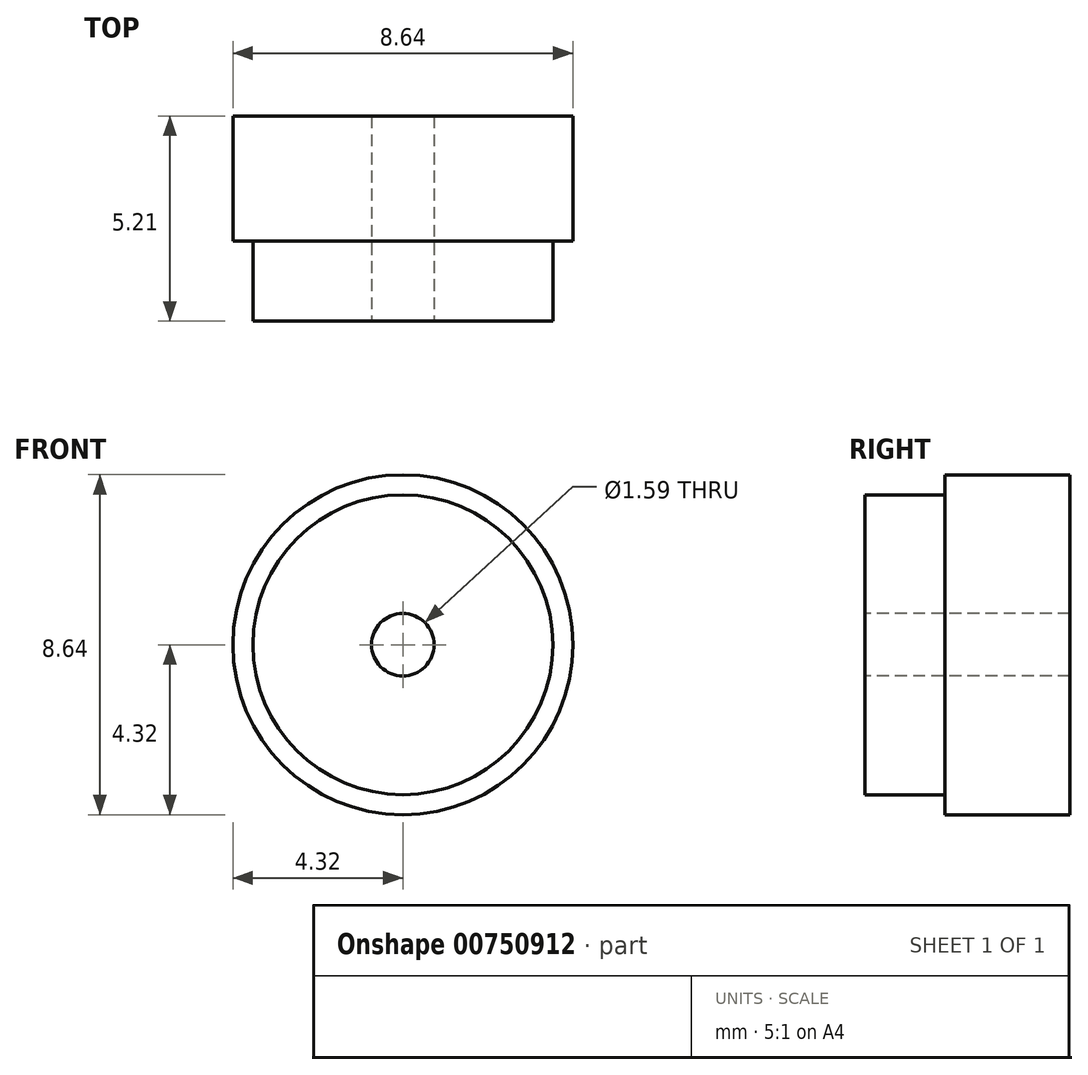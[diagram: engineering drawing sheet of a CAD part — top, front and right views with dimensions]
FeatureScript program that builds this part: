
annotation { "Feature Type Name" : "Feature", "Feature Type Description" : "" }
export const myFeature = defineFeature(function(context is Context, id is Id, definition is map)
    precondition{}
    {
        {
            var Q0;
            Q0=qCreatedBy(makeId("Front.planeOp"),FACE);
            var sketch = newSketch(context, id + "F0", { "sketchPlane" : qUnion([Q0])});
            skCircle(sketch, "E0", {"center": v(0, 0) * mm, "radius": 4.32 * mm});
            skSolve(sketch);
        }
        {
            var Q0;
            Q0 = qSketchRegion(id + "F0", true);
            extrude(context, id + "F1", {"entities" : qUnion([Q0]), "oppositeDirection" : true, "depth" : 3.17 * mm, "offsetDistance" : 25.4 * mm});
        }
        {
            var Q0;
            Q0=makeQuery(id+"F1.opExtrude","CAP_FACE",FACE,{"disambiguationData":[OSD([sQuery(id+"F0.wireOp",EDGE,"E0"),sQuery(id+"F0.wireOp",EDGE,"cbw0gS1s-dyO2-I5mG-PDLQ-LJ6yft7O6WXu")])],"isStart":true});
            var sketch = newSketch(context, id + "F2", { "sketchPlane" : qUnion([Q0])});
            skCircle(sketch, "E1", {"center": v(0, 0) * mm, "radius": 3.81 * mm});
            skSolve(sketch);
        }
        {
            var Q0;
            Q0 = qSketchRegion(id + "F2", true);
            extrude(context, id + "F3", {"entities" : qUnion([Q0]), "operationType" : NewBodyOperationType.ADD, "depth" : 2.03 * mm, "offsetDistance" : 25.4 * mm});
        }
        {
            var Q0;
            Q0=makeQuery(id+"F3.opExtrude","CAP_FACE",FACE,{"disambiguationData":[OSD([sQuery(id+"F2.wireOp",EDGE,"E1")])],"isStart":false});
            var sketch = newSketch(context, id + "F4", { "sketchPlane" : qUnion([Q0])});
            skCircle(sketch, "E2", {"center": v(0, 0) * mm, "radius": 0.8 * mm});
            skSolve(sketch);
        }
        {
            var Q0;
            Q0 = qSketchRegion(id + "F4", true);
            extrude(context, id + "F5", {"entities" : qUnion([Q0]), "operationType" : NewBodyOperationType.REMOVE, "endBound" : BoundingType.THROUGH_ALL, "oppositeDirection" : true, "depth" : 25.4 * mm, "offsetDistance" : 25.4 * mm});
        }
    });
